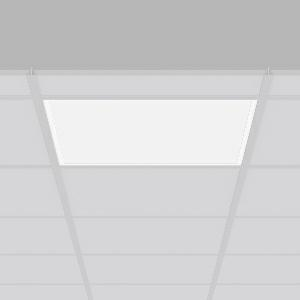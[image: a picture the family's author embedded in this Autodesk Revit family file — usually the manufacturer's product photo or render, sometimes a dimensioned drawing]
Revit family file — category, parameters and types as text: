
# Revit family: sidelite_eco_672359_002_1_72c1
name_source: partatom
category: Lighting Fixtures
units: mm (PartAtom-declared; Revit-internal decimal feet)

## family parameters
Cut with Voids When Loaded = No
Host = Face
Light Source = No
Part Type = Normal
Room Calculation Point = No
Round Connector Dimension = Use Diameter
Shared = No

## types (1)
- SIDELITE ECO (1 x LED Modul 840, 3700 lm, 4000)
    Apparent Load = 29 VA
    CIE Flux Codes = 46 79 96 100 100
    Color Rendering = 80
    Color Temperature = 4000
    Default Elevation = 1800 mm
    Description = Series: SIDELITE ECO
Highly economical recessed luminaire with progressive LED technology. For escape route illumination. Frame made of aluminium, powder-coated. Diffuser: plastic, opal. Lightguide and diffuser made of non-yellowing plastic (PMMA). Lateral light emission (RZB SIDELITE technology) for homogeneous light distribution. External driver. Self-contained system with automatic self-test. External driver with simple plug-in locking system. Extended connection cable (1.90 m). 
Colour: white
Length: 595 mm
Width: 595 mm
Cut-out length: 575 mm
Cut-out width: 575 mm
Recess height: 160 mm
Luminaire: recess height: 40 mm
Weight: 4.36 kg
Operating mode: maintained power mode
Duration time: 3 h
Lamp: LED
Socket: without socket
Colour temperature: 4000K
Colour rendering index (CRI): 80
System power: 29 W
Rated luminous flux: 3700 lm
Luminous flux, emergency: 410 lm
System power, emergency: -
Control gear: Regulated power supply
Protection class: I
Type of protection: IP 40
    Height = 0 mm  [stored 0 ft]
    Lamp = 1 x LED Modul 840
    Lamp Light Flux = 3700 lm
    Lamp count = 1
    Length = 595 mm
    Lifetime = 50000 h
    Luminous efficacy = 128 lm/W
    Manufacturer = RZB
    ModVariant = No
    Model = 672359.002.1
    Mounting Place = Ceiling
    Mounting Type = Recessed
    Number of Poles = 1
    OnlyDefault = Yes
    Power Factor = 1
    Product Name = SIDELITE ECO
    Product group = Recessed modular luminaires
    ProductGroupID = 406
    Protection Class = Protection class I
    Protection Degree = IP 40
    RLX_Detail_Level = 1
    RLX_Emergency_Light_Flux = 0 lm
    RLX_Emergency_Type = 0
    RLX_Emergency_Type_DB = No
    RlxData = <blob elided: 29189 chars, md5=a90ee603>
    Socket = socket
    Standby Power = 0 W
    System Light Flux = 3700 lm
    System Power = 29 W
    Type Comments = ALEA SPOT
    Type Image = 312272.002.jpg
    URL = http://relux.com
    VarID = ---
    Voltage = 230 V
    Voltage Range = 220-240 V
    Weight = 0.00 kg
    Width = 595 mm

note: [stored X ft] marks values corroborated as IEEE doubles in the binary element streams (Revit-internal decimal feet)

## geometry (parser evidence)
native form markers: Blend x4, Sweep x11
no freeform markers — native parametric forms only
